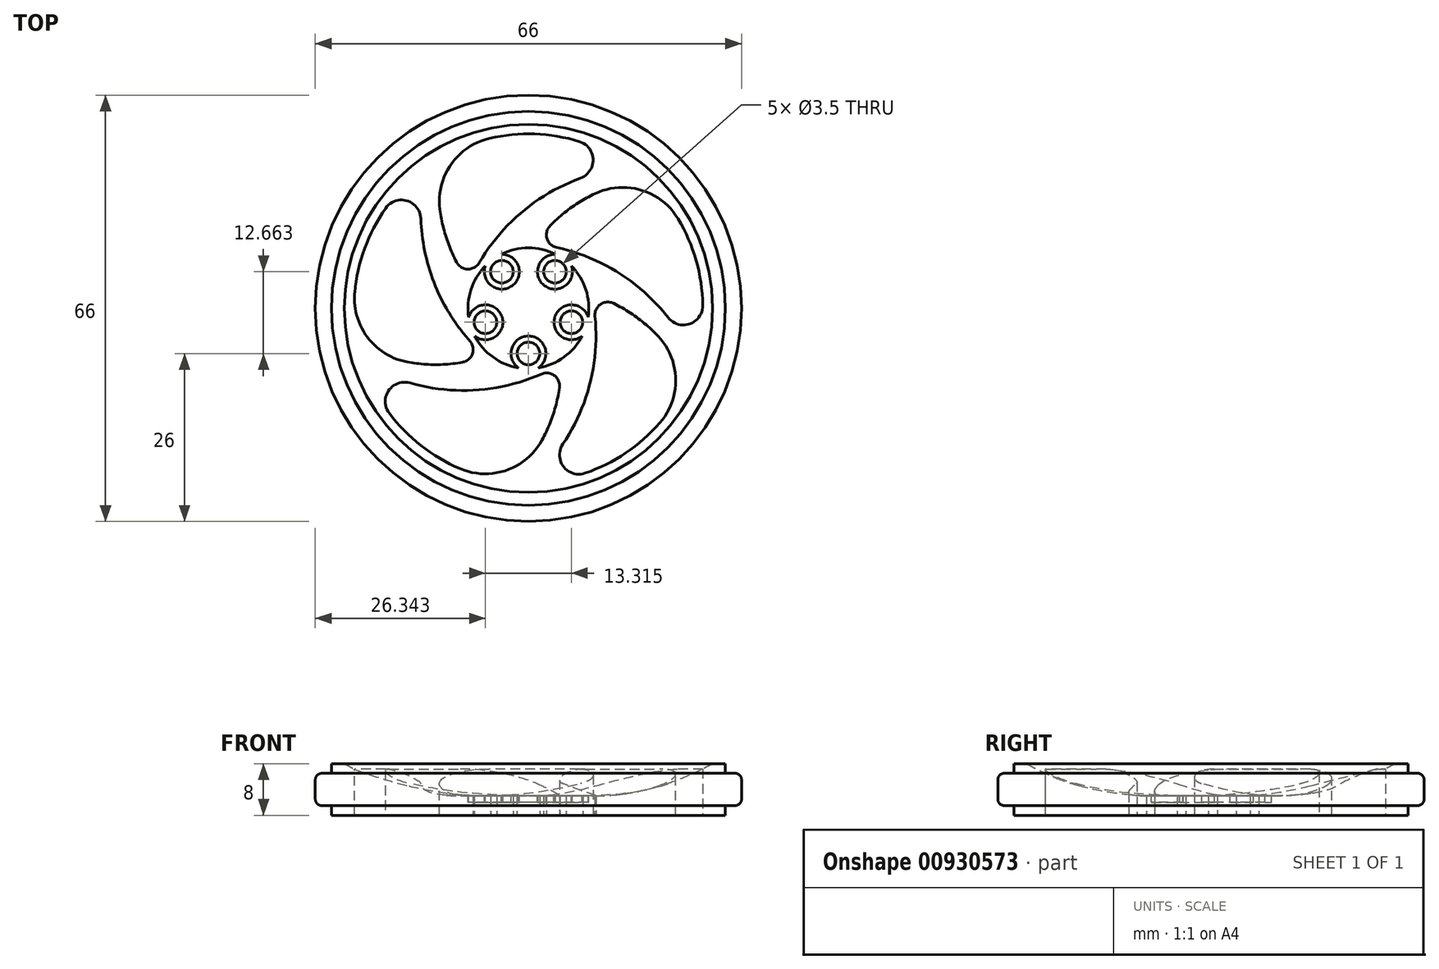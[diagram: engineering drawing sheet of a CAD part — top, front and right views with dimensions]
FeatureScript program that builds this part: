
annotation { "Feature Type Name" : "Feature", "Feature Type Description" : "" }
export const myFeature = defineFeature(function(context is Context, id is Id, definition is map)
    precondition{}
    {
        {
            var Q0;
            Q0=qCreatedBy(makeId("Front.planeOp"),FACE);
            var sketch = newSketch(context, id + "F0", { "sketchPlane" : qUnion([Q0])});
            skLineSegment(sketch, "E0.right", {"start": v(33, 1.5) * mm, "end": v(33, 6.5) * mm});
            skLineSegment(sketch, "E1", {"start": v(30.5, 6.5) * mm, "end": v(33, 6.5) * mm});
            skLineSegment(sketch, "E2", {"start": v(30.5, 6.5) * mm, "end": v(30.5, 8) * mm});
            skLineSegment(sketch, "E3.MirrorCS", {"start": v(30.5, 1.5) * mm, "end": v(30.5, 0) * mm});
            skLineSegment(sketch, "E4.MirrorCS", {"start": v(30.5, 1.5) * mm, "end": v(33, 1.5) * mm});
            skLineSegment(sketch, "E5.trimOffspring", {"start": v(28.5, 8) * mm, "end": v(30.5, 8) * mm});
            skLineSegment(sketch, "E6", {"start": v(0, 0) * mm, "end": v(30.5, 0) * mm});
            skLineSegment(sketch, "E7", {"start": v(0, 0) * mm, "end": v(0, 3) * mm});
            skLineSegment(sketch, "E8", {"start": v(0, 3) * mm, "end": v(10, 3) * mm});
            skArc(sketch, "E9", {"start": v(10, 3) * mm, "mid": v(19.58, 4.27) * mm, "end": v(28.5, 8) * mm});
            skSolve(sketch);
        }
        {
            var Q0;
            Q0=qSketchRegion(id+"F0",true);
            var Q1;
            Q1=sQuery(id+"F0.wireOp",EDGE,"E7");
            revolve(context, id + "F1", {"entities" : qUnion([Q0]), "axis" : qUnion([Q1]), "revolveType" : RevolveType.FULL});
        }
        {
            var Q0;
            Q0=makeQuery(id+"F1.opRevolve","SWEPT_EDGE",EDGE,{"disambiguationData":[OSD([sQuery(id+"F0.wireOp",EDGE,"E0.right"),sQuery(id+"F0.wireOp",EDGE,"E1")])]});
            var Q1;
            Q1=makeQuery(id+"F1.opRevolve","SWEPT_EDGE",EDGE,{"disambiguationData":[OSD([sQuery(id+"F0.wireOp",EDGE,"E0.right"),sQuery(id+"F0.wireOp",EDGE,"E4.MirrorCS")])]});
            fillet(context, id + "F2", {"entities" : qUnion([Q0, Q1]), "radius" : 1 * mm, "tangentPropagation" : true, "allowEdgeOverflow" : false});
        }
        {
            var Q0;
            Q0=makeQuery(id+"F1.opRevolve","SWEPT_FACE",FACE,{"disambiguationData":[OSD([sQuery(id+"F0.wireOp",EDGE,"E6")])]});
            var sketch = newSketch(context, id + "F3", { "sketchPlane" : qUnion([Q0])});
            skCircle(sketch, "E10", {"center": v(0, 0) * mm, "radius": 10 * mm, "construction": true});
            skCircle(sketch, "E11", {"center": v(0, 0) * mm, "radius": 28.5 * mm, "construction": true});
            skArc(sketch, "E12", {"start": v(-3, 26.83) * mm, "mid": v(-17.06, 20.93) * mm, "end": v(-25.68, 8.34) * mm});
            skArc(sketch, "E13.trimOffspring", {"start": v(-26.45, 5.44) * mm, "mid": v(-25.18, -9.76) * mm, "end": v(-15.87, -21.84) * mm});
            skArc(sketch, "E14.trimOffspring", {"start": v(18.2, -19.95) * mm, "mid": v(26.1, -6.9) * mm, "end": v(25.68, 8.34) * mm});
            skLineSegment(sketch, "E15", {"start": v(0, 28.5) * mm, "end": v(0, 0) * mm, "construction": true});
            skLineSegment(sketch, "E16", {"start": v(0, 0) * mm, "end": v(-25.68, 8.34) * mm, "construction": true});
            skLineSegment(sketch, "E17", {"start": v(0, 0) * mm, "end": v(25.68, 8.34) * mm, "construction": true});
            skLineSegment(sketch, "E18", {"start": v(0, 0) * mm, "end": v(-15.87, -21.84) * mm, "construction": true});
            skLineSegment(sketch, "E19", {"start": v(0, 0) * mm, "end": v(15.87, -21.84) * mm, "construction": true});
            skArc(sketch, "E20.trimOffspring", {"start": v(24.6, 11.14) * mm, "mid": v(14.63, 22.7) * mm, "end": v(0, 27) * mm});
            skArc(sketch, "E21.trimOffspring", {"start": v(-13.35, -23.47) * mm, "mid": v(1.5, -26.96) * mm, "end": v(15.87, -21.84) * mm});
            skCircle(sketch, "E22", {"center": v(0, 7) * mm, "radius": 1.75 * mm});
            skCircle(sketch, "E23", {"center": v(-4.11, -5.66) * mm, "radius": 1.75 * mm});
            skCircle(sketch, "E24", {"center": v(4.11, -5.66) * mm, "radius": 1.75 * mm});
            skCircle(sketch, "E25", {"center": v(6.66, 2.16) * mm, "radius": 1.75 * mm});
            skCircle(sketch, "E26", {"center": v(-6.66, 2.16) * mm, "radius": 1.75 * mm});
            skArc(sketch, "E27", {"start": v(9.77, -2.12) * mm, "mid": v(8.9, 13.79) * mm, "end": v(0, 27) * mm});
            skArc(sketch, "E28", {"start": v(1, -9.95) * mm, "mid": v(15.86, -4.2) * mm, "end": v(25.68, 8.34) * mm});
            skArc(sketch, "E29", {"start": v(-9.15, -4.03) * mm, "mid": v(0.9, -16.38) * mm, "end": v(15.87, -21.84) * mm});
            skArc(sketch, "E30", {"start": v(-6.66, 7.46) * mm, "mid": v(-15.3, -5.92) * mm, "end": v(-15.87, -21.84) * mm});
            skArc(sketch, "E31", {"start": v(5.04, 8.64) * mm, "mid": v(-10.36, 12.72) * mm, "end": v(-25.68, 8.34) * mm});
            skArc(sketch, "E32", {"start": v(-6.66, 7.46) * mm, "mid": v(-16.77, 8.6) * mm, "end": v(-26.45, 5.44) * mm});
            skArc(sketch, "E33", {"start": v(5.04, 8.64) * mm, "mid": v(3, 18.6) * mm, "end": v(-3, 26.83) * mm});
            skArc(sketch, "E34", {"start": v(9.77, -2.12) * mm, "mid": v(18.62, 2.9) * mm, "end": v(24.6, 11.14) * mm});
            skArc(sketch, "E35", {"start": v(1, -9.95) * mm, "mid": v(8.52, -16.81) * mm, "end": v(18.2, -19.95) * mm});
            skArc(sketch, "E36", {"start": v(-9.15, -4.03) * mm, "mid": v(-13.36, -13.3) * mm, "end": v(-13.35, -23.47) * mm});
            skSolve(sketch);
        }
        {
            var Q0;
            Q0=qSketchRegion(id+"F3",true);
            extrude(context, id + "F4", {"entities" : qUnion([Q0]), "operationType" : NewBodyOperationType.REMOVE, "oppositeDirection" : true, "depth" : 25 * mm});
        }
        {
            var Q0;
            Q0=makeQuery(id+"F4.boolean.opBoolean","COPY",EDGE,{"derivedFrom":makeQuery(id+"F4.opExtrude","SWEPT_EDGE",EDGE,{"disambiguationData":[OSD([sQuery(id+"F3.wireOp",EDGE,"E20.trimOffspring"),sQuery(id+"F3.wireOp",EDGE,"E27")])]})});
            var Q1;
            Q1=makeQuery(id+"F4.boolean.opBoolean","COPY",EDGE,{"derivedFrom":makeQuery(id+"F4.opExtrude","SWEPT_EDGE",EDGE,{"disambiguationData":[OSD([sQuery(id+"F3.wireOp",EDGE,"E12"),sQuery(id+"F3.wireOp",EDGE,"E31")])]})});
            var Q2;
            Q2=makeQuery(id+"F4.boolean.opBoolean","COPY",EDGE,{"derivedFrom":makeQuery(id+"F4.opExtrude","SWEPT_EDGE",EDGE,{"disambiguationData":[OSD([sQuery(id+"F3.wireOp",EDGE,"E13.trimOffspring"),sQuery(id+"F3.wireOp",EDGE,"E30")])]})});
            var Q3;
            Q3=makeQuery(id+"F4.boolean.opBoolean","COPY",EDGE,{"derivedFrom":makeQuery(id+"F4.opExtrude","SWEPT_EDGE",EDGE,{"disambiguationData":[OSD([sQuery(id+"F3.wireOp",EDGE,"E21.trimOffspring"),sQuery(id+"F3.wireOp",EDGE,"E29")])]})});
            var Q4;
            Q4=makeQuery(id+"F4.boolean.opBoolean","COPY",EDGE,{"derivedFrom":makeQuery(id+"F4.opExtrude","SWEPT_EDGE",EDGE,{"disambiguationData":[OSD([sQuery(id+"F3.wireOp",EDGE,"E14.trimOffspring"),sQuery(id+"F3.wireOp",EDGE,"E28")])]})});
            fillet(context, id + "F5", {"entities" : qUnion([Q0, Q1, Q2, Q3, Q4]), "radius" : 3 * mm, "tangentPropagation" : true, "allowEdgeOverflow" : false});
        }
        {
            var Q0;
            Q0=makeQuery(id+"F4.boolean.opBoolean","COPY",EDGE,{"derivedFrom":makeQuery(id+"F4.opExtrude","SWEPT_EDGE",EDGE,{"disambiguationData":[OSD([sQuery(id+"F3.wireOp",EDGE,"E14.trimOffspring"),sQuery(id+"F3.wireOp",EDGE,"E35")])]})});
            var Q1;
            Q1=makeQuery(id+"F4.boolean.opBoolean","COPY",EDGE,{"derivedFrom":makeQuery(id+"F4.opExtrude","SWEPT_EDGE",EDGE,{"disambiguationData":[OSD([sQuery(id+"F3.wireOp",EDGE,"E20.trimOffspring"),sQuery(id+"F3.wireOp",EDGE,"E34")])]})});
            var Q2;
            Q2=makeQuery(id+"F4.boolean.opBoolean","COPY",EDGE,{"derivedFrom":makeQuery(id+"F4.opExtrude","SWEPT_EDGE",EDGE,{"disambiguationData":[OSD([sQuery(id+"F3.wireOp",EDGE,"E12"),sQuery(id+"F3.wireOp",EDGE,"E33")])]})});
            var Q3;
            Q3=makeQuery(id+"F4.boolean.opBoolean","COPY",EDGE,{"derivedFrom":makeQuery(id+"F4.opExtrude","SWEPT_EDGE",EDGE,{"disambiguationData":[OSD([sQuery(id+"F3.wireOp",EDGE,"E13.trimOffspring"),sQuery(id+"F3.wireOp",EDGE,"E32")])]})});
            var Q4;
            Q4=makeQuery(id+"F4.boolean.opBoolean","COPY",EDGE,{"derivedFrom":makeQuery(id+"F4.opExtrude","SWEPT_EDGE",EDGE,{"disambiguationData":[OSD([sQuery(id+"F3.wireOp",EDGE,"E21.trimOffspring"),sQuery(id+"F3.wireOp",EDGE,"E36")])]})});
            fillet(context, id + "F6", {"entities" : qUnion([Q0, Q1, Q2, Q3, Q4]), "radius" : 10 * mm, "tangentPropagation" : true, "allowEdgeOverflow" : false});
        }
        {
            var Q0;
            Q0=makeQuery(id+"F4.boolean.opBoolean","COPY",EDGE,{"derivedFrom":makeQuery(id+"F4.opExtrude","SWEPT_EDGE",EDGE,{"disambiguationData":[OSD([sQuery(id+"F3.wireOp",EDGE,"E30"),sQuery(id+"F3.wireOp",EDGE,"E32")])]})});
            var Q1;
            Q1=makeQuery(id+"F4.boolean.opBoolean","COPY",EDGE,{"derivedFrom":makeQuery(id+"F4.opExtrude","SWEPT_EDGE",EDGE,{"disambiguationData":[OSD([sQuery(id+"F3.wireOp",EDGE,"E29"),sQuery(id+"F3.wireOp",EDGE,"E36")])]})});
            var Q2;
            Q2=makeQuery(id+"F4.boolean.opBoolean","COPY",EDGE,{"derivedFrom":makeQuery(id+"F4.opExtrude","SWEPT_EDGE",EDGE,{"disambiguationData":[OSD([sQuery(id+"F3.wireOp",EDGE,"E28"),sQuery(id+"F3.wireOp",EDGE,"E35")])]})});
            var Q3;
            Q3=makeQuery(id+"F4.boolean.opBoolean","COPY",EDGE,{"derivedFrom":makeQuery(id+"F4.opExtrude","SWEPT_EDGE",EDGE,{"disambiguationData":[OSD([sQuery(id+"F3.wireOp",EDGE,"E27"),sQuery(id+"F3.wireOp",EDGE,"E34")])]})});
            var Q4;
            Q4=makeQuery(id+"F4.boolean.opBoolean","COPY",EDGE,{"derivedFrom":makeQuery(id+"F4.opExtrude","SWEPT_EDGE",EDGE,{"disambiguationData":[OSD([sQuery(id+"F3.wireOp",EDGE,"E31"),sQuery(id+"F3.wireOp",EDGE,"E33")])]})});
            fillet(context, id + "F7", {"entities" : qUnion([Q0, Q1, Q2, Q3, Q4]), "radius" : 2 * mm, "tangentPropagation" : true, "allowEdgeOverflow" : false});
        }
        {
            var Q0;
            Q0=makeQuery(id+"F1.opRevolve","SWEPT_FACE",FACE,{"disambiguationData":[OSD([sQuery(id+"F0.wireOp",EDGE,"E8")])]});
            var sketch = newSketch(context, id + "F8", { "sketchPlane" : qUnion([Q0])});
            skArc(sketch, "E37", {"start": v(-6.66, 6.56) * mm, "mid": v(-2.53, 3.48) * mm, "end": v(-4.18, 8.36) * mm});
            skArc(sketch, "E38", {"start": v(4.18, 8.36) * mm, "mid": v(2.53, 3.48) * mm, "end": v(6.66, 6.56) * mm});
            skArc(sketch, "E39", {"start": v(9.25, -1.4) * mm, "mid": v(4.09, -1.33) * mm, "end": v(8.3, -4.3) * mm});
            skArc(sketch, "E40", {"start": v(1.53, -9.22) * mm, "mid": v(0, -4.3) * mm, "end": v(-1.53, -9.22) * mm});
            skArc(sketch, "E41", {"start": v(-8.3, -4.3) * mm, "mid": v(-4.09, -1.33) * mm, "end": v(-9.25, -1.4) * mm});
            skArc(sketch, "E42", {"start": v(-6.66, 6.56) * mm, "mid": v(-8.9, 2.89) * mm, "end": v(-9.25, -1.4) * mm});
            skArc(sketch, "E43.trimOffspring", {"start": v(4.18, 8.36) * mm, "mid": v(0, 9.35) * mm, "end": v(-4.18, 8.36) * mm});
            skArc(sketch, "E44.trimOffspring", {"start": v(9.25, -1.4) * mm, "mid": v(8.9, 2.89) * mm, "end": v(6.66, 6.56) * mm});
            skArc(sketch, "E45.trimOffspring", {"start": v(1.53, -9.22) * mm, "mid": v(5.5, -7.56) * mm, "end": v(8.3, -4.3) * mm});
            skArc(sketch, "E46.trimOffspring", {"start": v(-8.3, -4.3) * mm, "mid": v(-5.5, -7.56) * mm, "end": v(-1.53, -9.22) * mm});
            skSolve(sketch);
        }
        {
            var Q0;
            Q0=qSketchRegion(id+"F8",true);
            extrude(context, id + "F9", {"entities" : qUnion([Q0]), "operationType" : NewBodyOperationType.REMOVE, "oppositeDirection" : true, "depth" : 1 * mm});
        }
    });
